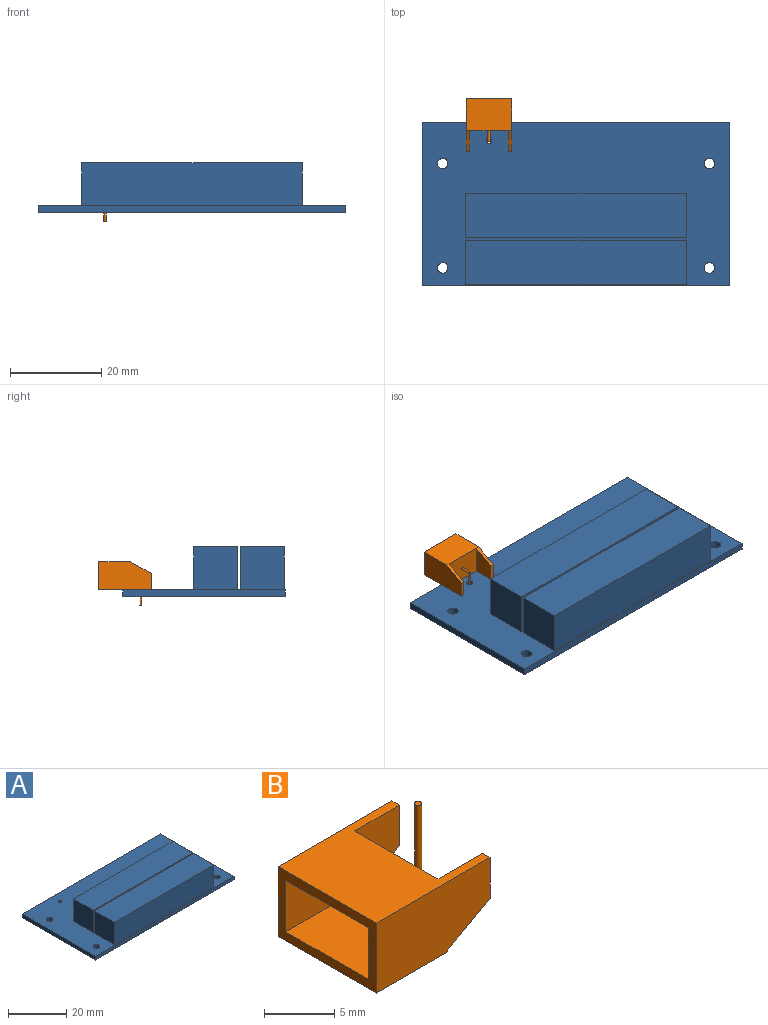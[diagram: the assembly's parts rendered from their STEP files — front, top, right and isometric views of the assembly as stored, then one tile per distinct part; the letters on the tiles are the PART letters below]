
ASSEMBLY  parts=2 mates=1
PART A: 21 faces, bbox 67.3x35.6x10.9 mm
  f0: plane 35.56x1.52mm, normal (-1,0,0), area 54.2mm2, adj f1,f3,f4,f19
  f1: plane 67.31x1.52mm, normal (0,-1,0), area 102.6mm2, adj f0,f2,f3,f4
  f2: plane 35.56x1.52mm, normal (1,0,0), area 54.2mm2, adj f1,f3,f4,f19
  f3: plane 67.31x35.56mm, normal (0,0,1), area 1444.2mm2, adj f0,f1,f2,f6,f7,f8,f9,f11
  f4: plane 67.31x35.56mm, normal (0,0,-1), area 2375.9mm2, adj f0,f1,f2,f15,f16,f17,f18,f19
  f5: plane 48.26x9.65mm, normal (0,0,1), area 465.8mm2, adj f6,f7,f8,f9
  f6: plane 9.65x9.4mm, normal (1,0,0), area 90.7mm2, adj f3,f5,f7,f9
  f7: plane 48.26x9.4mm, normal (0,1,0), area 453.5mm2, adj f3,f5,f6,f8
  f8: plane 9.65x9.4mm, normal (-1,0,0), area 90.7mm2, adj f3,f5,f7,f9
  f9: plane 48.26x9.4mm, normal (0,-1,0), area 453.5mm2, adj f3,f5,f6,f8
  f10: plane 48.26x9.65mm, normal (0,0,1), area 465.8mm2, adj f11,f12,f13,f14
  f11: plane 9.65x9.4mm, normal (1,0,0), area 90.7mm2, adj f3,f10,f12,f14
  f12: plane 48.26x9.4mm, normal (0,1,0), area 453.5mm2, adj f3,f10,f11,f13
  f13: plane 9.65x9.4mm, normal (-1,0,0), area 90.7mm2, adj f3,f10,f12,f14
  f14: plane 48.26x9.4mm, normal (0,-1,0), area 453.5mm2, adj f3,f10,f11,f13
  f15: cylinder r=1.14mm len=2.29mm, axis (0,0,1), area 10.9mm2, adj f3,f4
  f16: cylinder r=1.14mm len=2.29mm, axis (0,0,1), area 10.9mm2, adj f3,f4
  f17: cylinder r=1.14mm len=2.29mm, axis (0,0,1), area 10.9mm2, adj f3,f4
  f18: cylinder r=1.14mm len=2.29mm, axis (0,0,1), area 10.9mm2, adj f3,f4
  f19: plane 67.31x1.52mm, normal (0,1,0), area 102.6mm2, adj f0,f2,f3,f4
  f20: cylinder r=0.64mm len=1.52mm, axis (0,0,1), area 6.1mm2, adj f3,f4
PART B: 20 faces, bbox 11.5x9.9x9.5 mm
  f0: plane 9.9x6.1mm, normal (-1,0,0), area 23mm2, adj f3,f4,f5,f6,f15,f16,f17,f18
  f1: plane 3.56x0.75mm, normal (1,0,0), area 2.7mm2, adj f4,f6,f9,f13
  f2: plane 3.56x0.75mm, normal (1,0,0), area 2.7mm2, adj f4,f5,f7,f14
  f3: plane 9.9x7mm, normal (0,0,-1), area 69.3mm2, adj f0,f5,f6,f8,f13,f14
  f4: plane 11.5x9.9mm, normal (0,0,1), area 76.1mm2, adj f0,f1,f2,f5,f6,f7,f8,f9
  f5: plane 11.5x6.1mm, normal (0,1,0), area 64.4mm2, adj f0,f2,f3,f4,f14
  f6: plane 11.5x6.1mm, normal (0,-1,0), area 64.4mm2, adj f0,f1,f3,f4,f13
  f7: plane 6.1x4.5mm, normal (0,-1,0), area 21.7mm2, adj f2,f4,f8,f14
  f8: plane 8.4x6.1mm, normal (1,0,0), area 51mm2, adj f3,f4,f7,f9,f11
  f9: plane 6.1x4.5mm, normal (0,1,0), area 21.7mm2, adj f1,f4,f8,f13
  f10: plane 0.5x0.5mm, normal (0,0,1), area 0.2mm2, adj f12
  f11: cylinder r=0.25mm len=2.45mm, axis (-1,0,0), area 3.5mm2, adj f8,f12
  f12: cylinder r=0.25mm len=6.35mm, axis (0,0,-1), area 9.6mm2, adj f10,f11
  f13: plane 4.5x2.54mm, normal (0.49,0,-0.87), area 3.9mm2, adj f1,f3,f6,f9
  f14: plane 4.5x2.54mm, normal (0.49,0,-0.87), area 3.9mm2, adj f2,f3,f5,f7
  f15: plane 8.3x4.95mm, normal (0,0,-1), area 41.1mm2, adj f0,f16,f18,f19
  f16: plane 4.95x4.5mm, normal (0,-1,0), area 22.3mm2, adj f0,f15,f17,f19
  f17: plane 8.3x4.95mm, normal (0,0,1), area 41.1mm2, adj f0,f16,f18,f19
  f18: plane 4.95x4.5mm, normal (0,1,0), area 22.3mm2, adj f0,f15,f17,f19
  f19: plane 8.3x4.5mm, normal (-1,0,0), area 37.4mm2, adj f15,f16,f17,f18
PLACE A t=(-0.42,-21.01,15.13)mm
PLACE B rot(axis=(0.71,-0.71,0),180deg) t=(-53.13,19.86,22.76)mm
MATE fastened B.f12 <-> A.f20  axis (0,0,-1) through (-53.13,10.66,13.26)mm
